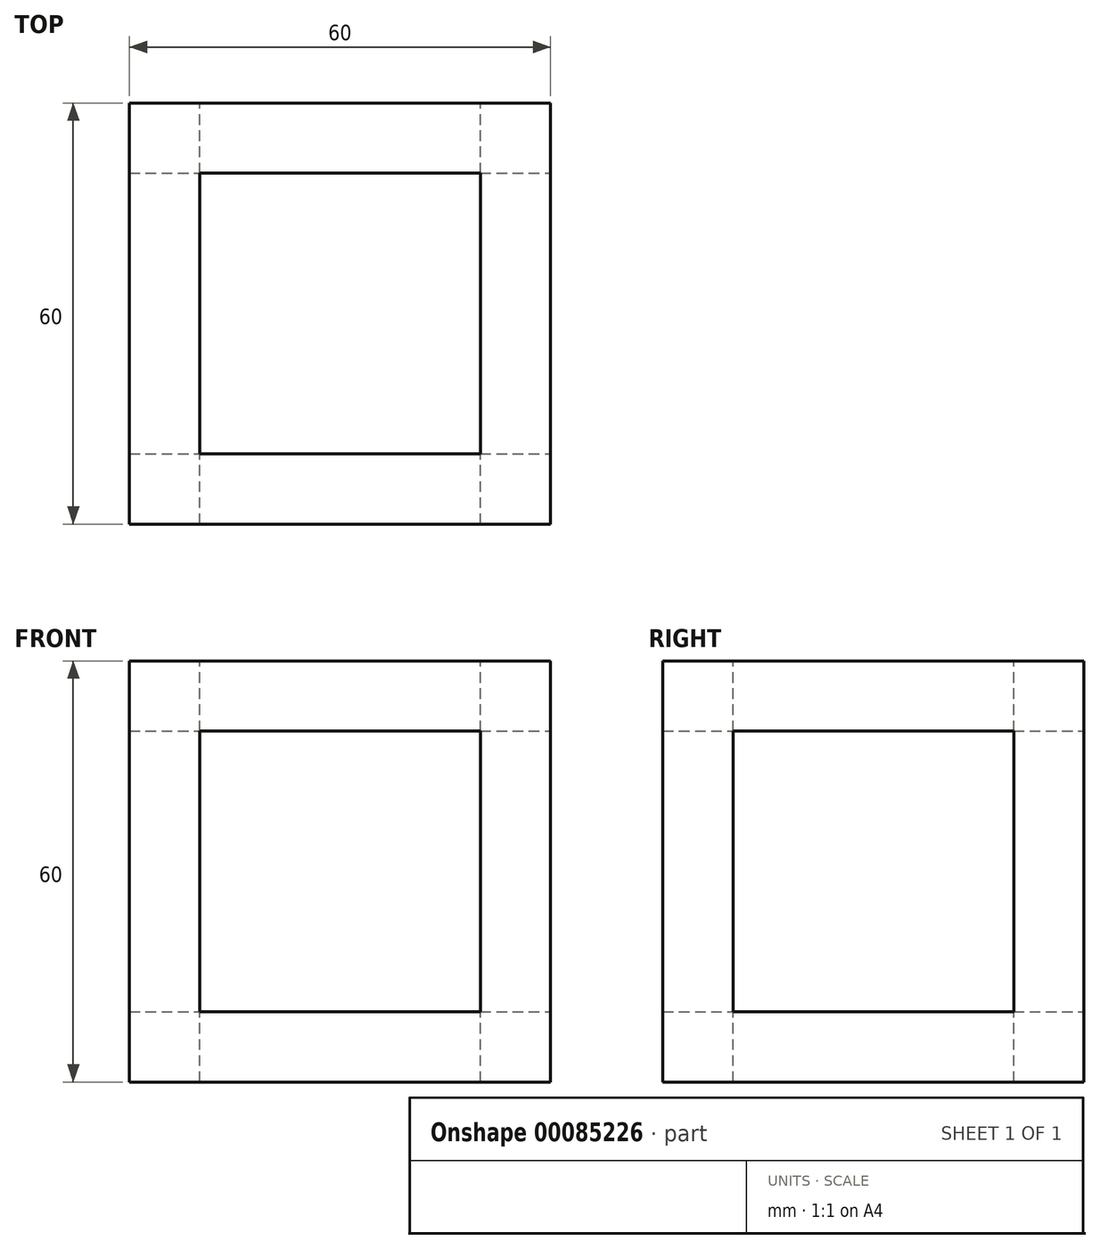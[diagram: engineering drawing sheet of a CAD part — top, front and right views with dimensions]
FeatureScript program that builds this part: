
annotation { "Feature Type Name" : "Feature", "Feature Type Description" : "" }
export const myFeature = defineFeature(function(context is Context, id is Id, definition is map)
    precondition{}
    {
        {
            var Q0;
            Q0=qCreatedBy(makeId("Front.planeOp"),FACE);
            var sketch = newSketch(context, id + "F0", { "sketchPlane" : qUnion([Q0])});
            skLineSegment(sketch, "E0", {"start": v(0, 56.08) * mm, "end": v(0, -49.32) * mm, "construction": true});
            skLineSegment(sketch, "E1", {"start": v(-57.8, 0) * mm, "end": v(65.66, 0) * mm, "construction": true});
            skLineSegment(sketch, "E2.bottom", {"start": v(-30, 30) * mm, "end": v(30, 30) * mm});
            skLineSegment(sketch, "E2.top", {"start": v(-30, -30) * mm, "end": v(30, -30) * mm});
            skLineSegment(sketch, "E2.left", {"start": v(-30, 30) * mm, "end": v(-30, -30) * mm});
            skLineSegment(sketch, "E2.right", {"start": v(30, 30) * mm, "end": v(30, -30) * mm});
            skLineSegment(sketch, "E3", {"start": v(-30, -30) * mm, "end": v(30, 30) * mm, "construction": true});
            skLineSegment(sketch, "E4", {"start": v(-30, 30) * mm, "end": v(30, -30) * mm, "construction": true});
            skPoint(sketch, "E5", {"position": v(0, 0) * mm});
            skLineSegment(sketch, "E6.bottom", {"start": v(-20, -20) * mm, "end": v(20, -20) * mm});
            skLineSegment(sketch, "E6.top", {"start": v(-20, 20) * mm, "end": v(20, 20) * mm});
            skLineSegment(sketch, "E6.left", {"start": v(-20, -20) * mm, "end": v(-20, 20) * mm});
            skLineSegment(sketch, "E6.right", {"start": v(20, -20) * mm, "end": v(20, 20) * mm});
            skLineSegment(sketch, "E7", {"start": v(-20, -20) * mm, "end": v(20, 20) * mm, "construction": true});
            skLineSegment(sketch, "E8", {"start": v(-20, 20) * mm, "end": v(20, -20) * mm, "construction": true});
            skSolve(sketch);
        }
        {
            var Q0;
            Q0 = qSketchRegion(id + "F0", true);
            extrude(context, id + "F1", {"entities" : qUnion([Q0]), "endBound" : BoundingType.SYMMETRIC, "depth" : 60 * mm});
        }
        {
            var Q0;
            Q0=makeQuery(id+"F1.opExtrude","SWEPT_FACE",FACE,{"disambiguationData":[OSD([sQuery(id+"F0.wireOp",EDGE,"E2.right")])]});
            var sketch = newSketch(context, id + "F2", { "sketchPlane" : qUnion([Q0])});
            skLineSegment(sketch, "E9.bottom", {"start": v(20, 20) * mm, "end": v(-20, 20) * mm});
            skLineSegment(sketch, "E9.top", {"start": v(20, -20) * mm, "end": v(-20, -20) * mm});
            skLineSegment(sketch, "E9.left", {"start": v(20, 20) * mm, "end": v(20, -20) * mm});
            skLineSegment(sketch, "E9.right", {"start": v(-20, 20) * mm, "end": v(-20, -20) * mm});
            skLineSegment(sketch, "E10", {"start": v(-20, 20) * mm, "end": v(20, -20) * mm, "construction": true});
            skLineSegment(sketch, "E11", {"start": v(20, 20) * mm, "end": v(-20, -20) * mm, "construction": true});
            skPoint(sketch, "E12", {"position": v(0, 0) * mm});
            skSolve(sketch);
        }
        {
            var Q0;
            Q0 = qSketchRegion(id + "F2", true);
            extrude(context, id + "F3", {"entities" : qUnion([Q0]), "operationType" : NewBodyOperationType.REMOVE, "endBound" : BoundingType.THROUGH_ALL, "oppositeDirection" : true, "depth" : 25 * mm});
        }
        {
            var Q0;
            Q0=makeQuery(id+"F1.opExtrude","SWEPT_FACE",FACE,{"disambiguationData":[OSD([sQuery(id+"F0.wireOp",EDGE,"E2.bottom")])]});
            var sketch = newSketch(context, id + "F4", { "sketchPlane" : qUnion([Q0])});
            skLineSegment(sketch, "E13.bottom", {"start": v(-20, 20) * mm, "end": v(20, 20) * mm});
            skLineSegment(sketch, "E13.top", {"start": v(-20, -20) * mm, "end": v(20, -20) * mm});
            skLineSegment(sketch, "E13.left", {"start": v(-20, 20) * mm, "end": v(-20, -20) * mm});
            skLineSegment(sketch, "E13.right", {"start": v(20, 20) * mm, "end": v(20, -20) * mm});
            skLineSegment(sketch, "E14", {"start": v(-20, -20) * mm, "end": v(20, 20) * mm, "construction": true});
            skLineSegment(sketch, "E15", {"start": v(-20, 20) * mm, "end": v(20, -20) * mm, "construction": true});
            skPoint(sketch, "E16", {"position": v(0, 0) * mm});
            skSolve(sketch);
        }
        {
            var Q0;
            Q0 = qSketchRegion(id + "F4", true);
            extrude(context, id + "F5", {"entities" : qUnion([Q0]), "operationType" : NewBodyOperationType.REMOVE, "endBound" : BoundingType.THROUGH_ALL, "oppositeDirection" : true, "depth" : 25 * mm});
        }
    });
